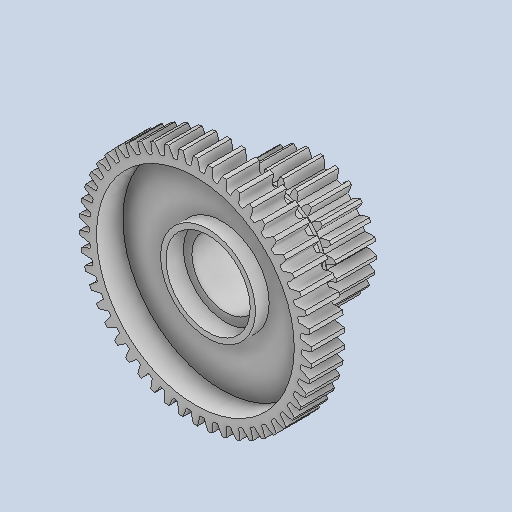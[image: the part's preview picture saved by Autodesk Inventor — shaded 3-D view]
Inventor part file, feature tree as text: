
AUTODESK INVENTOR PART (.ipt)
format: ipt  version: 2022.3 (Build 263350000, 350)  size: 620,032 bytes
history: native  units: in
note: dims shown in document units (in); Inventor stores cm internally (conversion verified against a paired STEP export)
features: chamfer x1
ambient origin geometry x8: Origin, YZ Plane, XZ Plane, XY Plane, X Axis, Y Axis, Z Axis, Center Point
bodies: Solid1 (feature_tree)
feature tree (1):
  chamfer  "Chamfer2"  [1 undecoded]
note: 1 required parameter value undecoded (feature->parameter linkage not recoverable at this tier; creation-order binding heuristic only, values carry confidence <= 0.55)
